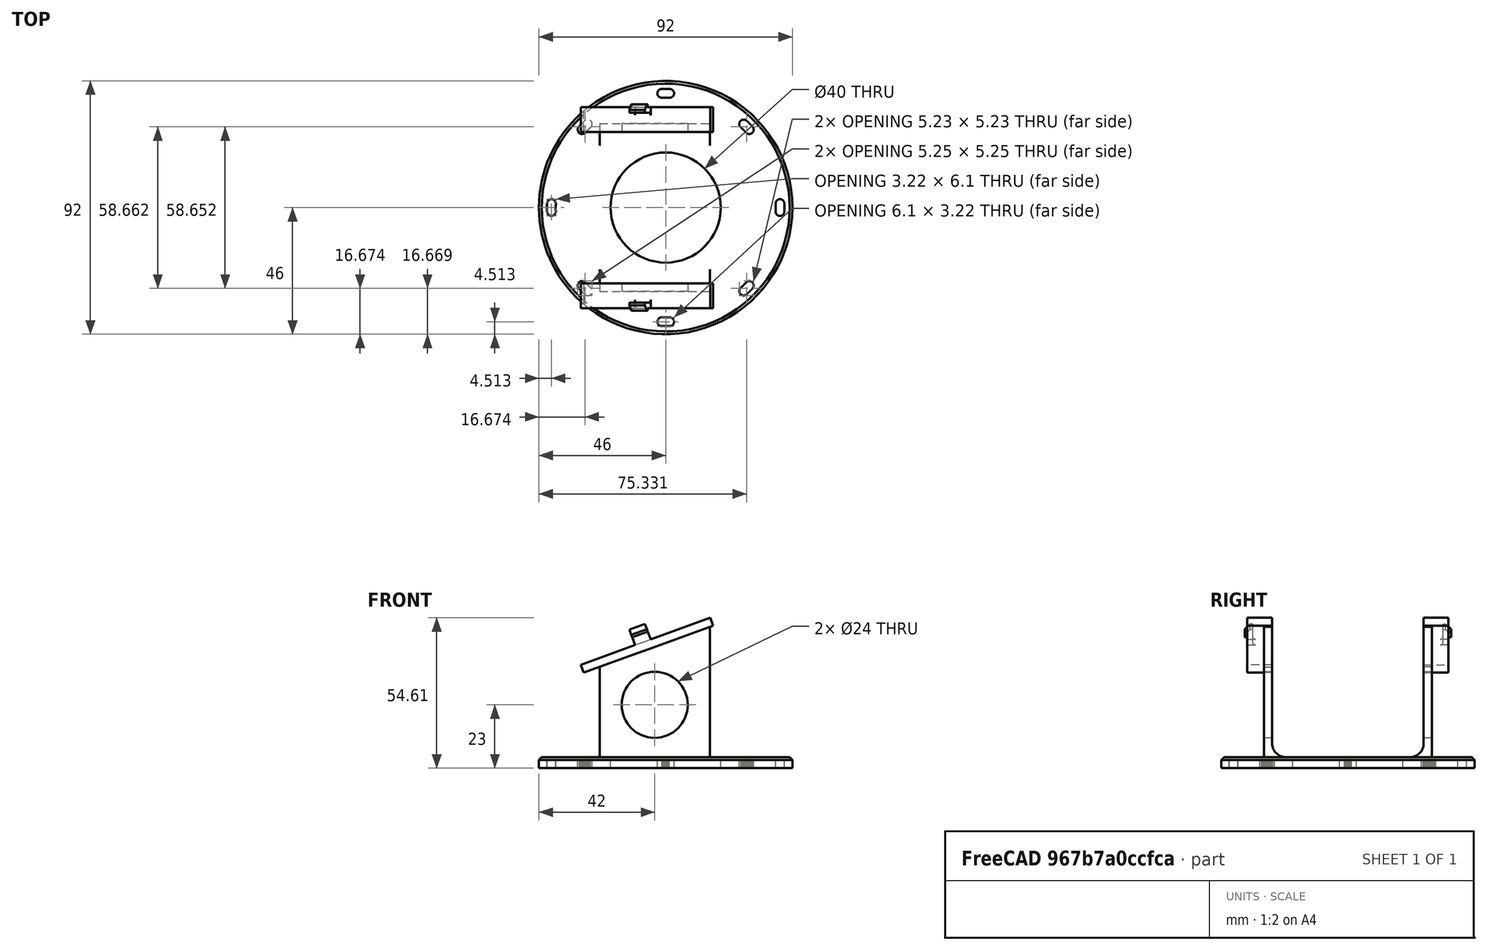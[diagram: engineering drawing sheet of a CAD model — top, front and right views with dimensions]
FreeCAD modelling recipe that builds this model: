
FCSTD DOCUMENT  (FreeCAD 0.15R4671 (Git))
Label: top_mount
License: All rights reserved
LicenseURL: http://en.wikipedia.org/wiki/All_rights_reserved
objects: Part::Cylinder×67, Part::MultiFuse×42, Part::Box×5, Part::Fillet×3, Part::Mirroring×2, Part::Cut×2, Part::Chamfer×2
note: 123 computed .brp shape members not serialized (recipe doc carries the construction recipe); baked Part::Feature solids carry a one-line shape summary decoded from their .brp

FEATURE [Part::Cylinder] Cylinder
  Angle = 360
  Height = 4
  Radius = 46
FEATURE [Part::Box] Box  label="Cube"
  Height = 50
  Length = 40
  Placement = pos=(-24,27.5,4) rot=(0,0,1;0rad)
  Width = 3
FEATURE [Part::Mirroring] Part__Mirroring  label="Cube (Mirror #1)"
  Base = (0,0,0)
  Normal = (0,1,0)
  Source = -> Box
FEATURE [Part::Box] Box001  label="Cube001"
  Height = 50
  Length = 100
  Placement = pos=(-70,-50,21) rot=(0,-1,0;0.349066rad)
  Width = 100
FEATURE [Part::MultiFuse] Fusion
  Shapes = -> [Cylinder,Part__Mirroring,Box]
FEATURE [Part::Cut] Cut
  Base = -> Fusion
  Tool = -> Box001
FEATURE [Part::Box] Box002  label="Cube002"
  Height = 3
  Length = 50
  Placement = pos=(-30,27.5,34) rot=(0,0,1;0rad)
  Width = 9
FEATURE [Part::Box] Box003  label="Cube003"
  Height = 6
  Length = 6
  Placement = pos=(-9,34.5,34) rot=(0,0,1;0rad)
  Width = 2
FEATURE [Part::Box] Box004  label="Cube004"
  Height = 3
  Length = 6
  Placement = pos=(-9,34.5,40) rot=(0,0,1;0rad)
  Width = 3
FEATURE [Part::MultiFuse] Fusion041
  Shapes = -> [Box004,Box003]
FEATURE [Part::Chamfer] Chamfer
  Base = -> Fusion041
  Edges = 1 edges r=2: [Edge2]
FEATURE [Part::MultiFuse] Fusion042
  Placement = pos=(10,0,13) rot=(0,-1,0;0.349066rad)
  Shapes = -> [Chamfer,Box002]
FEATURE [Part::Mirroring] Part__Mirroring001  label="Fusion042 (Mirror #2)"
  Base = (0,0,0)
  Normal = (0,1,0)
  Source = -> Fusion042
FEATURE [Part::MultiFuse] Fusion043
  Shapes = -> [Part__Mirroring001,Cut,Fusion042]
FEATURE [Part::Cylinder] Cylinder078
  Angle = 360
  Height = 10
  Radius = 20
FEATURE [Part::Cylinder] Cylinder079
  Angle = 360
  Height = 100
  Placement = pos=(-4,50,23) rot=(1,0,0;1.5708rad)
  Radius = 12
FEATURE [Part::Cylinder] Cylinder080
  Angle = 360
  Height = 10
  Placement = pos=(41.5,0,-2) rot=(0,0,1;0rad)
  Radius = 1.6
FEATURE [Part::Cylinder] Cylinder081
  Angle = 360
  Height = 10
  Placement = pos=(-41.5,0,-2) rot=(0,0,1;0rad)
  Radius = 1.6
FEATURE [Part::MultiFuse] Fusion044
  Placement = pos=(0,0,0) rot=(0,0,1;0.017453rad)
  Shapes = -> [Cylinder080,Cylinder081]
FEATURE [Part::Cylinder] Cylinder082
  Angle = 360
  Height = 10
  Placement = pos=(41.5,0,-2) rot=(0,0,1;0rad)
  Radius = 1.6
FEATURE [Part::Cylinder] Cylinder083
  Angle = 360
  Height = 10
  Placement = pos=(-41.5,0,-2) rot=(0,0,1;0rad)
  Radius = 1.6
FEATURE [Part::MultiFuse] Fusion045
  Placement = pos=(0,0,0) rot=(0,0,1;0.034907rad)
  Shapes = -> [Cylinder082,Cylinder083]
FEATURE [Part::Cylinder] Cylinder084
  Angle = 360
  Height = 10
  Placement = pos=(41.5,0,-2) rot=(0,0,1;0rad)
  Radius = 1.6
FEATURE [Part::Cylinder] Cylinder085
  Angle = 360
  Height = 10
  Placement = pos=(-41.5,0,-2) rot=(0,0,1;0rad)
  Radius = 1.6
FEATURE [Part::MultiFuse] Fusion046
  Placement = pos=(0,0,0) rot=(0,0,-1;0.017453rad)
  Shapes = -> [Cylinder084,Cylinder085]
FEATURE [Part::Cylinder] Cylinder086
  Angle = 360
  Height = 10
  Placement = pos=(41.5,0,-2) rot=(0,0,1;0rad)
  Radius = 1.6
FEATURE [Part::Cylinder] Cylinder087
  Angle = 360
  Height = 10
  Placement = pos=(-41.5,0,-2) rot=(0,0,1;0rad)
  Radius = 1.6
FEATURE [Part::MultiFuse] Fusion047
  Placement = pos=(0,0,0) rot=(0,0,-1;0.034907rad)
  Shapes = -> [Cylinder086,Cylinder087]
FEATURE [Part::Cylinder] Cylinder088
  Angle = 360
  Height = 10
  Placement = pos=(41.5,0,-2) rot=(0,0,1;0rad)
  Radius = 1.6
FEATURE [Part::Cylinder] Cylinder089
  Angle = 360
  Height = 10
  Placement = pos=(-41.5,0,-2) rot=(0,0,1;0rad)
  Radius = 1.6
FEATURE [Part::MultiFuse] Fusion048
  Placement = pos=(0,0,0) rot=(0,0,-1;0.008727rad)
  Shapes = -> [Cylinder088,Cylinder089]
FEATURE [Part::Cylinder] Cylinder090
  Angle = 360
  Height = 10
  Placement = pos=(41.5,0,-2) rot=(0,0,1;0rad)
  Radius = 1.6
FEATURE [Part::Cylinder] Cylinder091
  Angle = 360
  Height = 10
  Placement = pos=(-41.5,0,-2) rot=(0,0,1;0rad)
  Radius = 1.6
FEATURE [Part::MultiFuse] Fusion049
  Placement = pos=(0,0,0) rot=(0,0,-1;0.02618rad)
  Shapes = -> [Cylinder090,Cylinder091]
FEATURE [Part::Cylinder] Cylinder092
  Angle = 360
  Height = 10
  Placement = pos=(41.5,0,-2) rot=(0,0,1;0rad)
  Radius = 1.6
FEATURE [Part::Cylinder] Cylinder093
  Angle = 360
  Height = 10
  Placement = pos=(-41.5,0,-2) rot=(0,0,1;0rad)
  Radius = 1.6
FEATURE [Part::MultiFuse] Fusion050
  Placement = pos=(0,0,0) rot=(0,0,1;0.02618rad)
  Shapes = -> [Cylinder092,Cylinder093]
FEATURE [Part::Cylinder] Cylinder094
  Angle = 360
  Height = 10
  Placement = pos=(41.5,0,-2) rot=(0,0,1;0rad)
  Radius = 1.6
FEATURE [Part::Cylinder] Cylinder095
  Angle = 360
  Height = 10
  Placement = pos=(-41.5,0,-2) rot=(0,0,1;0rad)
  Radius = 1.6
FEATURE [Part::MultiFuse] Fusion051
  Placement = pos=(0,0,0) rot=(0,0,1;0.008727rad)
  Shapes = -> [Cylinder094,Cylinder095]
FEATURE [Part::MultiFuse] Fusion052
  Shapes = -> [Fusion047,Fusion050,Fusion045,Fusion049,Fusion046,Fusion048,Fusion044,Fusion051]
FEATURE [Part::Cylinder] Cylinder096
  Angle = 360
  Height = 10
  Placement = pos=(41.5,0,-2) rot=(0,0,1;0rad)
  Radius = 1.6
FEATURE [Part::Cylinder] Cylinder097
  Angle = 360
  Height = 10
  Placement = pos=(-41.5,0,-2) rot=(0,0,1;0rad)
  Radius = 1.6
FEATURE [Part::MultiFuse] Fusion053
  Placement = pos=(0,0,0) rot=(0,0,1;0.017453rad)
  Shapes = -> [Cylinder096,Cylinder097]
FEATURE [Part::Cylinder] Cylinder098
  Angle = 360
  Height = 10
  Placement = pos=(41.5,0,-2) rot=(0,0,1;0rad)
  Radius = 1.6
FEATURE [Part::Cylinder] Cylinder099
  Angle = 360
  Height = 10
  Placement = pos=(-41.5,0,-2) rot=(0,0,1;0rad)
  Radius = 1.6
FEATURE [Part::MultiFuse] Fusion054
  Placement = pos=(0,0,0) rot=(0,0,1;0.034907rad)
  Shapes = -> [Cylinder098,Cylinder099]
FEATURE [Part::Cylinder] Cylinder100
  Angle = 360
  Height = 10
  Placement = pos=(41.5,0,-2) rot=(0,0,1;0rad)
  Radius = 1.6
FEATURE [Part::Cylinder] Cylinder101
  Angle = 360
  Height = 10
  Placement = pos=(-41.5,0,-2) rot=(0,0,1;0rad)
  Radius = 1.6
FEATURE [Part::MultiFuse] Fusion055
  Placement = pos=(0,0,0) rot=(0,0,-1;0.017453rad)
  Shapes = -> [Cylinder100,Cylinder101]
FEATURE [Part::Cylinder] Cylinder102
  Angle = 360
  Height = 10
  Placement = pos=(41.5,0,-2) rot=(0,0,1;0rad)
  Radius = 1.6
FEATURE [Part::Cylinder] Cylinder103
  Angle = 360
  Height = 10
  Placement = pos=(-41.5,0,-2) rot=(0,0,1;0rad)
  Radius = 1.6
FEATURE [Part::MultiFuse] Fusion056
  Placement = pos=(0,0,0) rot=(0,0,-1;0.034907rad)
  Shapes = -> [Cylinder102,Cylinder103]
FEATURE [Part::Cylinder] Cylinder104
  Angle = 360
  Height = 10
  Placement = pos=(41.5,0,-2) rot=(0,0,1;0rad)
  Radius = 1.6
FEATURE [Part::Cylinder] Cylinder105
  Angle = 360
  Height = 10
  Placement = pos=(-41.5,0,-2) rot=(0,0,1;0rad)
  Radius = 1.6
FEATURE [Part::MultiFuse] Fusion057
  Placement = pos=(0,0,0) rot=(0,0,-1;0.008727rad)
  Shapes = -> [Cylinder104,Cylinder105]
FEATURE [Part::Cylinder] Cylinder106
  Angle = 360
  Height = 10
  Placement = pos=(41.5,0,-2) rot=(0,0,1;0rad)
  Radius = 1.6
FEATURE [Part::Cylinder] Cylinder107
  Angle = 360
  Height = 10
  Placement = pos=(-41.5,0,-2) rot=(0,0,1;0rad)
  Radius = 1.6
FEATURE [Part::MultiFuse] Fusion058
  Placement = pos=(0,0,0) rot=(0,0,-1;0.02618rad)
  Shapes = -> [Cylinder106,Cylinder107]
FEATURE [Part::Cylinder] Cylinder108
  Angle = 360
  Height = 10
  Placement = pos=(41.5,0,-2) rot=(0,0,1;0rad)
  Radius = 1.6
FEATURE [Part::Cylinder] Cylinder109
  Angle = 360
  Height = 10
  Placement = pos=(-41.5,0,-2) rot=(0,0,1;0rad)
  Radius = 1.6
FEATURE [Part::MultiFuse] Fusion059
  Placement = pos=(0,0,0) rot=(0,0,1;0.02618rad)
  Shapes = -> [Cylinder108,Cylinder109]
FEATURE [Part::Cylinder] Cylinder110
  Angle = 360
  Height = 10
  Placement = pos=(41.5,0,-2) rot=(0,0,1;0rad)
  Radius = 1.6
FEATURE [Part::Cylinder] Cylinder111
  Angle = 360
  Height = 10
  Placement = pos=(-41.5,0,-2) rot=(0,0,1;0rad)
  Radius = 1.6
FEATURE [Part::MultiFuse] Fusion060
  Placement = pos=(0,0,0) rot=(0,0,1;0.008727rad)
  Shapes = -> [Cylinder110,Cylinder111]
FEATURE [Part::MultiFuse] Fusion061
  Placement = pos=(0,0,0) rot=(0,0,1;0.785398rad)
  Shapes = -> [Fusion056,Fusion059,Fusion054,Fusion058,Fusion055,Fusion057,Fusion053,Fusion060]
FEATURE [Part::Cylinder] Cylinder112
  Angle = 360
  Height = 10
  Placement = pos=(41.5,0,-2) rot=(0,0,1;0rad)
  Radius = 1.6
FEATURE [Part::Cylinder] Cylinder113
  Angle = 360
  Height = 10
  Placement = pos=(-41.5,0,-2) rot=(0,0,1;0rad)
  Radius = 1.6
FEATURE [Part::MultiFuse] Fusion062
  Placement = pos=(0,0,0) rot=(0,0,1;0.017453rad)
  Shapes = -> [Cylinder112,Cylinder113]
FEATURE [Part::Cylinder] Cylinder114
  Angle = 360
  Height = 10
  Placement = pos=(41.5,0,-2) rot=(0,0,1;0rad)
  Radius = 1.6
FEATURE [Part::Cylinder] Cylinder115
  Angle = 360
  Height = 10
  Placement = pos=(-41.5,0,-2) rot=(0,0,1;0rad)
  Radius = 1.6
FEATURE [Part::MultiFuse] Fusion063
  Placement = pos=(0,0,0) rot=(0,0,1;0.034907rad)
  Shapes = -> [Cylinder114,Cylinder115]
FEATURE [Part::Cylinder] Cylinder116
  Angle = 360
  Height = 10
  Placement = pos=(41.5,0,-2) rot=(0,0,1;0rad)
  Radius = 1.6
FEATURE [Part::Cylinder] Cylinder117
  Angle = 360
  Height = 10
  Placement = pos=(-41.5,0,-2) rot=(0,0,1;0rad)
  Radius = 1.6
FEATURE [Part::MultiFuse] Fusion064
  Placement = pos=(0,0,0) rot=(0,0,-1;0.017453rad)
  Shapes = -> [Cylinder116,Cylinder117]
FEATURE [Part::Cylinder] Cylinder118
  Angle = 360
  Height = 10
  Placement = pos=(41.5,0,-2) rot=(0,0,1;0rad)
  Radius = 1.6
FEATURE [Part::Cylinder] Cylinder119
  Angle = 360
  Height = 10
  Placement = pos=(-41.5,0,-2) rot=(0,0,1;0rad)
  Radius = 1.6
FEATURE [Part::MultiFuse] Fusion065
  Placement = pos=(0,0,0) rot=(0,0,-1;0.034907rad)
  Shapes = -> [Cylinder118,Cylinder119]
FEATURE [Part::Cylinder] Cylinder120
  Angle = 360
  Height = 10
  Placement = pos=(41.5,0,-2) rot=(0,0,1;0rad)
  Radius = 1.6
FEATURE [Part::Cylinder] Cylinder121
  Angle = 360
  Height = 10
  Placement = pos=(-41.5,0,-2) rot=(0,0,1;0rad)
  Radius = 1.6
FEATURE [Part::MultiFuse] Fusion066
  Placement = pos=(0,0,0) rot=(0,0,-1;0.008727rad)
  Shapes = -> [Cylinder120,Cylinder121]
FEATURE [Part::Cylinder] Cylinder122
  Angle = 360
  Height = 10
  Placement = pos=(41.5,0,-2) rot=(0,0,1;0rad)
  Radius = 1.6
FEATURE [Part::Cylinder] Cylinder123
  Angle = 360
  Height = 10
  Placement = pos=(-41.5,0,-2) rot=(0,0,1;0rad)
  Radius = 1.6
FEATURE [Part::MultiFuse] Fusion067
  Placement = pos=(0,0,0) rot=(0,0,-1;0.02618rad)
  Shapes = -> [Cylinder122,Cylinder123]
FEATURE [Part::Cylinder] Cylinder124
  Angle = 360
  Height = 10
  Placement = pos=(41.5,0,-2) rot=(0,0,1;0rad)
  Radius = 1.6
FEATURE [Part::Cylinder] Cylinder125
  Angle = 360
  Height = 10
  Placement = pos=(-41.5,0,-2) rot=(0,0,1;0rad)
  Radius = 1.6
FEATURE [Part::MultiFuse] Fusion068
  Placement = pos=(0,0,0) rot=(0,0,1;0.02618rad)
  Shapes = -> [Cylinder124,Cylinder125]
FEATURE [Part::Cylinder] Cylinder126
  Angle = 360
  Height = 10
  Placement = pos=(41.5,0,-2) rot=(0,0,1;0rad)
  Radius = 1.6
FEATURE [Part::Cylinder] Cylinder127
  Angle = 360
  Height = 10
  Placement = pos=(-41.5,0,-2) rot=(0,0,1;0rad)
  Radius = 1.6
FEATURE [Part::MultiFuse] Fusion069
  Placement = pos=(0,0,0) rot=(0,0,1;0.008727rad)
  Shapes = -> [Cylinder126,Cylinder127]
FEATURE [Part::MultiFuse] Fusion070
  Placement = pos=(0,0,0) rot=(0,0,-1;0.785398rad)
  Shapes = -> [Fusion065,Fusion068,Fusion063,Fusion067,Fusion064,Fusion066,Fusion062,Fusion069]
FEATURE [Part::Cylinder] Cylinder128
  Angle = 360
  Height = 10
  Placement = pos=(41.5,0,-2) rot=(0,0,1;0rad)
  Radius = 1.6
FEATURE [Part::Cylinder] Cylinder129
  Angle = 360
  Height = 10
  Placement = pos=(-41.5,0,-2) rot=(0,0,1;0rad)
  Radius = 1.6
FEATURE [Part::MultiFuse] Fusion071
  Placement = pos=(0,0,0) rot=(0,0,1;0.017453rad)
  Shapes = -> [Cylinder128,Cylinder129]
FEATURE [Part::Cylinder] Cylinder130
  Angle = 360
  Height = 10
  Placement = pos=(41.5,0,-2) rot=(0,0,1;0rad)
  Radius = 1.6
FEATURE [Part::Cylinder] Cylinder131
  Angle = 360
  Height = 10
  Placement = pos=(-41.5,0,-2) rot=(0,0,1;0rad)
  Radius = 1.6
FEATURE [Part::MultiFuse] Fusion072
  Placement = pos=(0,0,0) rot=(0,0,1;0.034907rad)
  Shapes = -> [Cylinder130,Cylinder131]
FEATURE [Part::Cylinder] Cylinder132
  Angle = 360
  Height = 10
  Placement = pos=(41.5,0,-2) rot=(0,0,1;0rad)
  Radius = 1.6
FEATURE [Part::Cylinder] Cylinder133
  Angle = 360
  Height = 10
  Placement = pos=(-41.5,0,-2) rot=(0,0,1;0rad)
  Radius = 1.6
FEATURE [Part::MultiFuse] Fusion073
  Placement = pos=(0,0,0) rot=(0,0,-1;0.017453rad)
  Shapes = -> [Cylinder132,Cylinder133]
FEATURE [Part::Cylinder] Cylinder134
  Angle = 360
  Height = 10
  Placement = pos=(41.5,0,-2) rot=(0,0,1;0rad)
  Radius = 1.6
FEATURE [Part::Cylinder] Cylinder135
  Angle = 360
  Height = 10
  Placement = pos=(-41.5,0,-2) rot=(0,0,1;0rad)
  Radius = 1.6
FEATURE [Part::MultiFuse] Fusion074
  Placement = pos=(0,0,0) rot=(0,0,-1;0.034907rad)
  Shapes = -> [Cylinder134,Cylinder135]
FEATURE [Part::Cylinder] Cylinder136
  Angle = 360
  Height = 10
  Placement = pos=(41.5,0,-2) rot=(0,0,1;0rad)
  Radius = 1.6
FEATURE [Part::Cylinder] Cylinder137
  Angle = 360
  Height = 10
  Placement = pos=(-41.5,0,-2) rot=(0,0,1;0rad)
  Radius = 1.6
FEATURE [Part::MultiFuse] Fusion075
  Placement = pos=(0,0,0) rot=(0,0,-1;0.008727rad)
  Shapes = -> [Cylinder136,Cylinder137]
FEATURE [Part::Cylinder] Cylinder138
  Angle = 360
  Height = 10
  Placement = pos=(41.5,0,-2) rot=(0,0,1;0rad)
  Radius = 1.6
FEATURE [Part::Cylinder] Cylinder139
  Angle = 360
  Height = 10
  Placement = pos=(-41.5,0,-2) rot=(0,0,1;0rad)
  Radius = 1.6
FEATURE [Part::MultiFuse] Fusion076
  Placement = pos=(0,0,0) rot=(0,0,-1;0.02618rad)
  Shapes = -> [Cylinder138,Cylinder139]
FEATURE [Part::Cylinder] Cylinder140
  Angle = 360
  Height = 10
  Placement = pos=(41.5,0,-2) rot=(0,0,1;0rad)
  Radius = 1.6
FEATURE [Part::Cylinder] Cylinder141
  Angle = 360
  Height = 10
  Placement = pos=(-41.5,0,-2) rot=(0,0,1;0rad)
  Radius = 1.6
FEATURE [Part::MultiFuse] Fusion077
  Placement = pos=(0,0,0) rot=(0,0,1;0.02618rad)
  Shapes = -> [Cylinder140,Cylinder141]
FEATURE [Part::Cylinder] Cylinder142
  Angle = 360
  Height = 10
  Placement = pos=(41.5,0,-2) rot=(0,0,1;0rad)
  Radius = 1.6
FEATURE [Part::Cylinder] Cylinder143
  Angle = 360
  Height = 10
  Placement = pos=(-41.5,0,-2) rot=(0,0,1;0rad)
  Radius = 1.6
FEATURE [Part::MultiFuse] Fusion078
  Placement = pos=(0,0,0) rot=(0,0,1;0.008727rad)
  Shapes = -> [Cylinder142,Cylinder143]
FEATURE [Part::MultiFuse] Fusion079
  Placement = pos=(0,0,0) rot=(0,0,1;1.5708rad)
  Shapes = -> [Fusion074,Fusion077,Fusion072,Fusion076,Fusion073,Fusion075,Fusion071,Fusion078]
FEATURE [Part::MultiFuse] Fusion080
  Shapes = -> [Fusion079,Fusion070,Fusion052,Fusion061]
FEATURE [Part::MultiFuse] Fusion081
  Shapes = -> [Cylinder079,Cylinder078,Fusion080]
FEATURE [Part::Cut] Cut001
  Base = -> Fusion043
  Tool = -> Fusion081
FEATURE [Part::Chamfer] Chamfer001
  Base = -> Cut001
  Edges = 1 edges r=1: [Edge62]
FEATURE [Part::Fillet] Fillet
  Base = -> Chamfer001
  Edges = 2 edges r=5: [Edge116,Edge141]
FEATURE [Part::Fillet] Fillet001
  Base = -> Fillet
  Edges = 1 edges r=1: [Edge631]
FEATURE [Part::Fillet] Fillet002
  Base = -> Fillet001
  Edges = 1 edges r=1: [Edge658]
